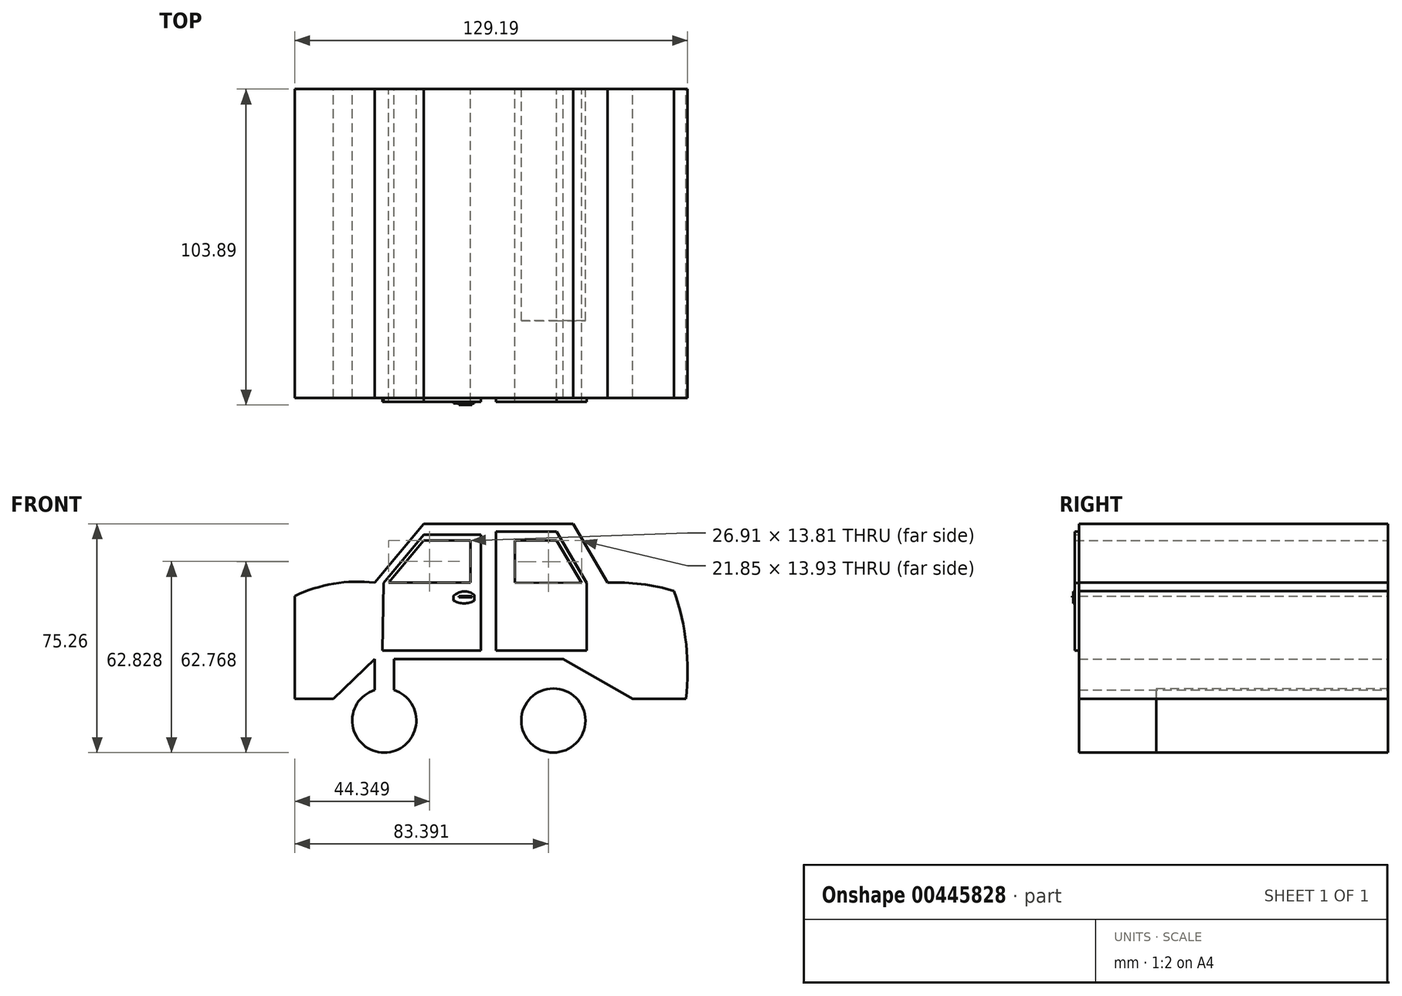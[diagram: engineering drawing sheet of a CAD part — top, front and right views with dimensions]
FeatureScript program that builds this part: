
annotation { "Feature Type Name" : "Feature", "Feature Type Description" : "" }
export const myFeature = defineFeature(function(context is Context, id is Id, definition is map)
    precondition{}
    {
        {
            var Q0;
            Q0=qCreatedBy(makeId("Front.planeOp"),FACE);
            var sketch = newSketch(context, id + "F0", { "sketchPlane" : qUnion([Q0])});
            skLineSegment(sketch, "E0", {"start": v(-16.12, 13.11) * mm, "end": v(45.84, 13.11) * mm});
            skLineSegment(sketch, "E1.MirrorCS", {"start": v(45.84, 13.11) * mm, "end": v(-16.12, 13.11) * mm});
            skLineSegment(sketch, "E2", {"start": v(-16.12, 13.11) * mm, "end": v(-16.12, -7.08) * mm});
            skLineSegment(sketch, "E3", {"start": v(-16.12, -7.08) * mm, "end": v(-9.76, -7.08) * mm});
            skLineSegment(sketch, "E4", {"start": v(-9.76, -7.08) * mm, "end": v(-9.76, 13.11) * mm});
            skCircle(sketch, "E5", {"center": v(-12.94, -7.08) * mm, "radius": 10.54 * mm});
            skCircle(sketch, "E6.MirrorC", {"center": v(42.66, -7.08) * mm, "radius": 10.54 * mm});
            skLineSegment(sketch, "E7.MirrorCS", {"start": v(45.84, -7.08) * mm, "end": v(39.48, -7.08) * mm});
            skLineSegment(sketch, "E8.MirrorCS", {"start": v(39.48, -7.08) * mm, "end": v(39.48, 13.11) * mm});
            skLineSegment(sketch, "E9.MirrorCS", {"start": v(45.84, 13.11) * mm, "end": v(45.84, -7.08) * mm});
            skLineSegment(sketch, "E10", {"start": v(-16.12, 13.11) * mm, "end": v(-29.67, 0) * mm});
            skLineSegment(sketch, "E11", {"start": v(-29.67, 0) * mm, "end": v(-42.4, 0) * mm});
            skLineSegment(sketch, "E12", {"start": v(-42.4, 0) * mm, "end": v(-42.4, 33.86) * mm});
            skLineSegment(sketch, "E13", {"start": v(-16.12, 38.28) * mm, "end": v(0, 57.64) * mm});
            skLineSegment(sketch, "E14", {"start": v(0, 57.64) * mm, "end": v(49.16, 57.64) * mm});
            skLineSegment(sketch, "E15", {"start": v(49.16, 57.64) * mm, "end": v(60.5, 38.28) * mm});
            skArc(sketch, "E16", {"start": v(-16.12, 38.28) * mm, "mid": v(-29.57, 37.9) * mm, "end": v(-42.4, 33.86) * mm});
            skArc(sketch, "E17", {"start": v(82.35, 35.52) * mm, "mid": v(71.54, 37.78) * mm, "end": v(60.5, 38.28) * mm});
            skLineSegment(sketch, "E18", {"start": v(45.84, 13.11) * mm, "end": v(68.8, 0) * mm});
            skLineSegment(sketch, "E19", {"start": v(68.8, 0) * mm, "end": v(86.22, 0) * mm});
            skArc(sketch, "E20", {"start": v(86.22, 0) * mm, "mid": v(86.34, 17.98) * mm, "end": v(82.35, 35.52) * mm});
            skLineSegment(sketch, "E21", {"start": v(0, 52.11) * mm, "end": v(-11.5, 38.3) * mm});
            skLineSegment(sketch, "E22", {"start": v(-11.5, 38.3) * mm, "end": v(15.41, 38.3) * mm});
            skLineSegment(sketch, "E23", {"start": v(15.41, 38.3) * mm, "end": v(15.41, 52.11) * mm});
            skLineSegment(sketch, "E24", {"start": v(15.41, 52.11) * mm, "end": v(0, 52.11) * mm});
            skLineSegment(sketch, "E25", {"start": v(30.07, 52.11) * mm, "end": v(30.07, 38.3) * mm});
            skLineSegment(sketch, "E26", {"start": v(30.07, 38.3) * mm, "end": v(51.93, 38.18) * mm});
            skLineSegment(sketch, "E27", {"start": v(51.93, 38.18) * mm, "end": v(43.77, 52.11) * mm});
            skLineSegment(sketch, "E28", {"start": v(43.77, 52.11) * mm, "end": v(30.07, 52.11) * mm});
            skSolve(sketch);
        }
        {
            var Q0;
            {var subQ4=sQuery(id+"F0.wireOp",EDGE,"E10");Q0=makeQuery(id+"F0.imprint","IMPRINT",FACE,{"disambiguationData":[TD([[makeQuery(id+"F0.imprint","IMPRINT",EDGE,{"derivedFrom":subQ4}),-1.0]])]});}
            var Q1;
            {var subQ0=sQuery(id+"F0.wireOp",EDGE,"E3");Q1=makeQuery(id+"F0.imprint","IMPRINT",FACE,{"disambiguationData":[TD([[makeQuery(id+"F0.imprint","IMPRINT",EDGE,{"derivedFrom":subQ0}),-1.0]])]});}
            var Q2;
            {var subQ0=sQuery(id+"F0.wireOp",EDGE,"E3");Q2=makeQuery(id+"F0.imprint","IMPRINT",FACE,{"disambiguationData":[TD([[makeQuery(id+"F0.imprint","IMPRINT",EDGE,{"derivedFrom":subQ0}),1.0]])]});}
            var Q3;
            {var subQ1=sQuery(id+"F0.wireOp",EDGE,"E1.MirrorCS");var subQ3=sQuery(id+"F0.wireOp",EDGE,"E4");var subQ4=makeQuery(id+"F0.imprint","INTERSECT",VERTEX,{"derivedFrom":[subQ1,subQ3]});Q3=makeQuery(id+"F0.imprint","IMPRINT",FACE,{"disambiguationData":[TD([[makeQuery(id+"F0.imprint","IMPRINT",EDGE,{"disambiguationData":[TD([[subQ4,1.0]])],"derivedFrom":subQ3}),1.0]])]});}
            var Q4;
            {var subQ0=sQuery(id+"F0.wireOp",EDGE,"E7.MirrorCS");Q4=makeQuery(id+"F0.imprint","IMPRINT",FACE,{"disambiguationData":[TD([[makeQuery(id+"F0.imprint","IMPRINT",EDGE,{"derivedFrom":subQ0}),1.0]])]});}
            var Q5;
            {var subQ0=sQuery(id+"F0.wireOp",EDGE,"E7.MirrorCS");Q5=makeQuery(id+"F0.imprint","IMPRINT",FACE,{"disambiguationData":[TD([[makeQuery(id+"F0.imprint","IMPRINT",EDGE,{"derivedFrom":subQ0}),-1.0]])]});}
            var Q6;
            {var subQ3=sQuery(id+"F0.wireOp",EDGE,"E8.MirrorCS");var subQ5=sQuery(id+"F0.wireOp",EDGE,"E6.MirrorC");var subQ7=makeQuery(id+"F0.imprint","INTERSECT",VERTEX,{"derivedFrom":[subQ5,subQ3]});Q6=makeQuery(id+"F0.imprint","IMPRINT",FACE,{"disambiguationData":[TD([[makeQuery(id+"F0.imprint","IMPRINT",EDGE,{"disambiguationData":[TD([[subQ7,-1.0]])],"derivedFrom":subQ5}),1.0]])]});}
            extrude(context, id + "F1", {"entities" : qUnion([Q0, Q1, Q2, Q3, Q4, Q5, Q6]), "depth" : 76.2 * mm});
        }
        {
            var Q0;
            Q0=makeQuery(id+"F1.opExtrude","CAP_FACE",FACE,{"disambiguationData":[OSD([sQuery(id+"F0.wireOp",EDGE,"E1.MirrorCS"),sQuery(id+"F0.wireOp",EDGE,"E2"),sQuery(id+"F0.wireOp",EDGE,"E4"),sQuery(id+"F0.wireOp",EDGE,"E5"),sQuery(id+"F0.wireOp",EDGE,"E6.MirrorC"),sQuery(id+"F0.wireOp",EDGE,"E8.MirrorCS"),sQuery(id+"F0.wireOp",EDGE,"E9.MirrorCS"),sQuery(id+"F0.wireOp",EDGE,"E10"),sQuery(id+"F0.wireOp",EDGE,"E11"),sQuery(id+"F0.wireOp",EDGE,"E12"),sQuery(id+"F0.wireOp",EDGE,"E13"),sQuery(id+"F0.wireOp",EDGE,"E14"),sQuery(id+"F0.wireOp",EDGE,"E15"),sQuery(id+"F0.wireOp",EDGE,"E16"),sQuery(id+"F0.wireOp",EDGE,"E17"),sQuery(id+"F0.wireOp",EDGE,"E18"),sQuery(id+"F0.wireOp",EDGE,"E19"),sQuery(id+"F0.wireOp",EDGE,"E20"),sQuery(id+"F0.wireOp",EDGE,"E21"),sQuery(id+"F0.wireOp",EDGE,"E22"),sQuery(id+"F0.wireOp",EDGE,"E23"),sQuery(id+"F0.wireOp",EDGE,"E24"),sQuery(id+"F0.wireOp",EDGE,"E25"),sQuery(id+"F0.wireOp",EDGE,"E26"),sQuery(id+"F0.wireOp",EDGE,"E27"),sQuery(id+"F0.wireOp",EDGE,"E28")])],"isStart":false});
            extrude(context, id + "F2", {"entities" : qUnion([Q0]), "operationType" : NewBodyOperationType.ADD, "depth" : 25.4 * mm});
        }
        {
            var Q0;
            Q0=makeQuery(id+"F2.opExtrude","CAP_FACE",FACE,{"disambiguationData":[OSD([sQuery(id+"F0.wireOp",EDGE,"E1.MirrorCS"),sQuery(id+"F0.wireOp",EDGE,"E2"),sQuery(id+"F0.wireOp",EDGE,"E4"),sQuery(id+"F0.wireOp",EDGE,"E5"),sQuery(id+"F0.wireOp",EDGE,"E6.MirrorC"),sQuery(id+"F0.wireOp",EDGE,"E8.MirrorCS"),sQuery(id+"F0.wireOp",EDGE,"E9.MirrorCS"),sQuery(id+"F0.wireOp",EDGE,"E10"),sQuery(id+"F0.wireOp",EDGE,"E11"),sQuery(id+"F0.wireOp",EDGE,"E12"),sQuery(id+"F0.wireOp",EDGE,"E13"),sQuery(id+"F0.wireOp",EDGE,"E14"),sQuery(id+"F0.wireOp",EDGE,"E15"),sQuery(id+"F0.wireOp",EDGE,"E16"),sQuery(id+"F0.wireOp",EDGE,"E17"),sQuery(id+"F0.wireOp",EDGE,"E18"),sQuery(id+"F0.wireOp",EDGE,"E19"),sQuery(id+"F0.wireOp",EDGE,"E20"),sQuery(id+"F0.wireOp",EDGE,"E21"),sQuery(id+"F0.wireOp",EDGE,"E22"),sQuery(id+"F0.wireOp",EDGE,"E23"),sQuery(id+"F0.wireOp",EDGE,"E24"),sQuery(id+"F0.wireOp",EDGE,"E25"),sQuery(id+"F0.wireOp",EDGE,"E26"),sQuery(id+"F0.wireOp",EDGE,"E27"),sQuery(id+"F0.wireOp",EDGE,"E28")])],"isStart":false});
            var sketch = newSketch(context, id + "F3", { "sketchPlane" : qUnion([Q0])});
            skLineSegment(sketch, "E29", {"start": v(18.8, 54.77) * mm, "end": v(18.8, 15.99) * mm});
            skLineSegment(sketch, "E30", {"start": v(18.8, 15.99) * mm, "end": v(-13.52, 15.99) * mm});
            skLineSegment(sketch, "E31", {"start": v(-13.52, 15.99) * mm, "end": v(-13.19, 38.18) * mm});
            skLineSegment(sketch, "E32", {"start": v(-13.19, 38.18) * mm, "end": v(0, 54.03) * mm});
            skLineSegment(sketch, "E33", {"start": v(0, 54.03) * mm, "end": v(18.8, 54.03) * mm});
            skSolve(sketch);
        }
        {
            var Q0;
            {var subQ0=sQuery(id+"F3.wireOp",EDGE,"E30");Q0=makeQuery(id+"F3.imprint","IMPRINT",FACE,{"disambiguationData":[TD([[makeQuery(id+"F3.imprint","IMPRINT",EDGE,{"derivedFrom":subQ0}),-1.0]])]});}
            extrude(context, id + "F4", {"entities" : qUnion([Q0]), "operationType" : NewBodyOperationType.ADD, "depth" : 1.27 * mm});
        }
        {
            var Q0;
            Q0=makeQuery(id+"F2.opExtrude","CAP_FACE",FACE,{"disambiguationData":[OSD([sQuery(id+"F0.wireOp",EDGE,"E1.MirrorCS"),sQuery(id+"F0.wireOp",EDGE,"E2"),sQuery(id+"F0.wireOp",EDGE,"E4"),sQuery(id+"F0.wireOp",EDGE,"E5"),sQuery(id+"F0.wireOp",EDGE,"E6.MirrorC"),sQuery(id+"F0.wireOp",EDGE,"E8.MirrorCS"),sQuery(id+"F0.wireOp",EDGE,"E9.MirrorCS"),sQuery(id+"F0.wireOp",EDGE,"E10"),sQuery(id+"F0.wireOp",EDGE,"E11"),sQuery(id+"F0.wireOp",EDGE,"E12"),sQuery(id+"F0.wireOp",EDGE,"E13"),sQuery(id+"F0.wireOp",EDGE,"E14"),sQuery(id+"F0.wireOp",EDGE,"E15"),sQuery(id+"F0.wireOp",EDGE,"E16"),sQuery(id+"F0.wireOp",EDGE,"E17"),sQuery(id+"F0.wireOp",EDGE,"E18"),sQuery(id+"F0.wireOp",EDGE,"E19"),sQuery(id+"F0.wireOp",EDGE,"E20"),sQuery(id+"F0.wireOp",EDGE,"E21"),sQuery(id+"F0.wireOp",EDGE,"E22"),sQuery(id+"F0.wireOp",EDGE,"E23"),sQuery(id+"F0.wireOp",EDGE,"E24"),sQuery(id+"F0.wireOp",EDGE,"E25"),sQuery(id+"F0.wireOp",EDGE,"E26"),sQuery(id+"F0.wireOp",EDGE,"E27"),sQuery(id+"F0.wireOp",EDGE,"E28")])],"isStart":false});
            var sketch = newSketch(context, id + "F5", { "sketchPlane" : qUnion([Q0])});
            skLineSegment(sketch, "E34", {"start": v(23.73, 54.03) * mm, "end": v(23.73, 15.99) * mm});
            skLineSegment(sketch, "E35", {"start": v(23.73, 15.99) * mm, "end": v(53.65, 15.99) * mm});
            skLineSegment(sketch, "E36", {"start": v(53.65, 15.99) * mm, "end": v(53.65, 38.18) * mm});
            skLineSegment(sketch, "E37", {"start": v(53.65, 38.18) * mm, "end": v(43.77, 55.05) * mm});
            skLineSegment(sketch, "E38", {"start": v(43.77, 55.05) * mm, "end": v(23.73, 55.05) * mm});
            skLineSegment(sketch, "E39", {"start": v(23.73, 55.05) * mm, "end": v(23.73, 54.03) * mm});
            skSolve(sketch);
        }
        {
            var Q0;
            Q0=makeQuery(id+"F5.imprint","IMPRINT",FACE,{"disambiguationData":[TD([[makeQuery(id+"F5.imprint","IMPRINT",EDGE,{"derivedFrom":sQuery(id+"F5.wireOp",EDGE,"E34")}),1.0]])]});
            extrude(context, id + "F6", {"entities" : qUnion([Q0]), "operationType" : NewBodyOperationType.ADD, "depth" : 1.27 * mm});
        }
        {
            var Q0;
            Q0=makeQuery(id+"F4.opExtrude","CAP_FACE",FACE,{"disambiguationData":[OSD([sQuery(id+"F0.wireOp",EDGE,"E21"),sQuery(id+"F0.wireOp",EDGE,"E22"),sQuery(id+"F0.wireOp",EDGE,"E23"),sQuery(id+"F0.wireOp",EDGE,"E24"),sQuery(id+"F3.wireOp",EDGE,"E29"),sQuery(id+"F3.wireOp",EDGE,"E30"),sQuery(id+"F3.wireOp",EDGE,"E31"),sQuery(id+"F3.wireOp",EDGE,"E32"),sQuery(id+"F3.wireOp",EDGE,"E33")])],"isStart":false});
            var sketch = newSketch(context, id + "F7", { "sketchPlane" : qUnion([Q0])});
            skArc(sketch, "E40", {"start": v(16.72, 34.17) * mm, "mid": v(13.24, 35.35) * mm, "end": v(9.86, 33.93) * mm});
            skLineSegment(sketch, "E41", {"start": v(9.86, 33.93) * mm, "end": v(9.86, 32.35) * mm});
            skLineSegment(sketch, "E42", {"start": v(16.72, 34.17) * mm, "end": v(16.72, 32.35) * mm});
            skArc(sketch, "E43", {"start": v(9.86, 32.35) * mm, "mid": v(13.29, 31.46) * mm, "end": v(16.72, 32.35) * mm});
            skLineSegment(sketch, "E44", {"start": v(11.65, 33.79) * mm, "end": v(15.9, 33.79) * mm});
            skLineSegment(sketch, "E45", {"start": v(15.9, 33.79) * mm, "end": v(15.9, 33.4) * mm});
            skLineSegment(sketch, "E46", {"start": v(15.9, 33.4) * mm, "end": v(11.65, 33.4) * mm});
            skLineSegment(sketch, "E47", {"start": v(11.65, 33.4) * mm, "end": v(11.65, 33.79) * mm});
            skSolve(sketch);
        }
        {
            var Q0;
            Q0=makeQuery(id+"F7.imprint","IMPRINT",FACE,{"disambiguationData":[TD([[makeQuery(id+"F7.imprint","IMPRINT",EDGE,{"derivedFrom":sQuery(id+"F7.wireOp",EDGE,"E44")}),-1.0]])]});
            var sketch = newSketch(context, id + "F8", { "sketchPlane" : qUnion([Q0])});
            skSolve(sketch);
        }
        {
            var Q0;
            Q0=makeQuery(id+"F7.imprint","IMPRINT",FACE,{"disambiguationData":[TD([[makeQuery(id+"F7.imprint","IMPRINT",EDGE,{"derivedFrom":sQuery(id+"F7.wireOp",EDGE,"E40")}),1.0]])]});
            extrude(context, id + "F9", {"entities" : qUnion([Q0]), "operationType" : NewBodyOperationType.ADD, "depth" : 0.5 * mm});
        }
        {
            var Q0;
            Q0=makeQuery(id+"F8.imprint","IMPRINT",FACE,{"disambiguationData":[TD([[makeQuery(id+"F8.imprint","IMPRINT",EDGE,{"derivedFrom":makeQuery(id+"F7.imprint","IMPRINT",EDGE,{"derivedFrom":sQuery(id+"F7.wireOp",EDGE,"E44")})}),-1.0]])]});
            extrude(context, id + "F10", {"entities" : qUnion([Q0]), "operationType" : NewBodyOperationType.ADD, "depth" : 1.02 * mm});
        }
    });
